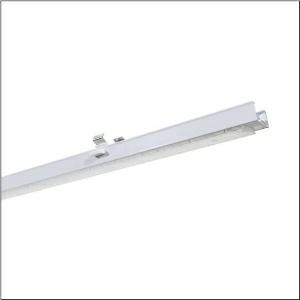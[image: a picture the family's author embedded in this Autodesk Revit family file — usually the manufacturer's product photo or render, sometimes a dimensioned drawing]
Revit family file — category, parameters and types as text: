
# Revit family: sanierungs-leuchteneinsatz_31_gen_2_51re18mb4cb_d75b
name_source: partatom
category: Lighting Fixtures
units: mm (PartAtom-declared; Revit-internal decimal feet)

## family parameters
Cut with Voids When Loaded = No
Host = Face
Light Source = No
Part Type = Normal
Room Calculation Point = No
Round Connector Dimension = Use Diameter
Shared = No

## types (1)
- --- (1 x LED, 11500 lm, 66 W, 4000K)
    Apparent Load = 66 VA
    CIE Flux Codes = 71 89 97 97 100
    Color Rendering = 80
    Color Temperature = 4000K
    Default Elevation = 1800 mm
    Description = Refurbishment luminaire insert Gen.2, luminaire insert, of extruded aluminium section, coated, traffic white (RAL 9016), length: 1.472mm, width: 91mm, height: 53mm, LED rated luminous flux: 11.500lm, light colour: 840, control gear: ON/OFF Multilumen, control gear: ECG Multilumen, with system connector: socket, mains connection: 220..240V, AC, 50/60Hz, connected load according to luminous flux setting (19/24/32/37/47/52/60/66W), luminous flux adjustable on luminaire in eight steps (3450/4380/5800/6700/8350/9200/10500/11500lm ), primary light control with lens, of plastic, primary optical cover: cover, of PMMA, light emission: direct distribution, protection rating (complete): IP20, insulation class (complete): insulation class I (protective earthing), certification: CE, UKCA, permissible ambient temperature for indoor applications: -20..+40°C, packaging unit: 1 piece
    Height = 58 mm
    Lamp = 1 x LED
    Lamp Light Flux = 11500 lm
    Lamp Power = 66 W
    Lamp count = 1
    Length = 1472 mm
    Luminous efficacy = 174 lm/W
    Manufacturer = Siteco
    ModVariant = No
    Model = 51RE18MB4CB
    Mounting Place = Ceiling
    Mounting Type = Pendant
    Number of Poles = 1
    OnlyDefault = Yes
    Power Factor = 1
    Product Name = Sanierungs-Leuchteneinsatz 31 Gen.2
    Product group = luminaire insert
    ProductGroupID = 902
    Protection Class = Protection class I
    Protection Degree = IP 20
    RLX_Detail_Level = 1
    RlxData = <blob elided: 21165 chars, md5=d1e97410>
    Socket = socket
    Standby Power = 0 W
    System Light Flux = 11500 lm
    System Power = 66 W
    Type Comments = factory setting: luminous flux: 100 % | (ON | ON | ON)
    Type Image = l_1266702.jpg
    URL = http://relux.com
    VarID = @adj_067961
    Voltage = 0 V
    Weight = 0.00 kg
    Width = 65 mm

## geometry (parser evidence)
native form markers: Blend x4, Sweep x13
no freeform markers — native parametric forms only
